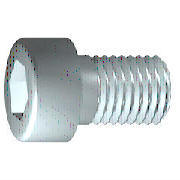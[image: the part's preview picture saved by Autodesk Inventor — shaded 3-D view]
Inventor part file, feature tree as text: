
AUTODESK INVENTOR PART (.ipt)
format: ipt  version: 2017 (Build 210142000, 142)  size: 181,760 bytes
history: native  units: mm (DEFAULTED — no unit token found)
features: sketch x2, extrude x1, plane x1, fillet x1
ambient origin geometry x7: Origin, YZ Plane, XY Plane, X Axis, Y Axis, Z Axis, Center Point
bodies: Solid1 (feature_tree), Body (feature_tree)
feature tree (5):
  extrude  "Slot"  Depth=5.0mm
  plane  "Work Plane1"
  fillet  "Fillet2"  Radius=5.0mm
  sketch  "Sketch1"  dims[d1=22.0mm d2=0.49086mm d3=5.0mm]
  sketch  "Sketch2"  dims[d4=2.5mm d5=60.0deg d6=5.0mm d7=5.0mm d8=4.618802mm d9=8.5mm d10=90.0deg d11=10.0mm d12=0.0mm d13=22.0mm d14=0.0mm d15=0.49076mm d16=0.49076mm d17=0.5mm d19=0.0mm d26=55.0mm d27=45.0deg d28=0.0mm d29=0.0mm d30=0.1mm]
